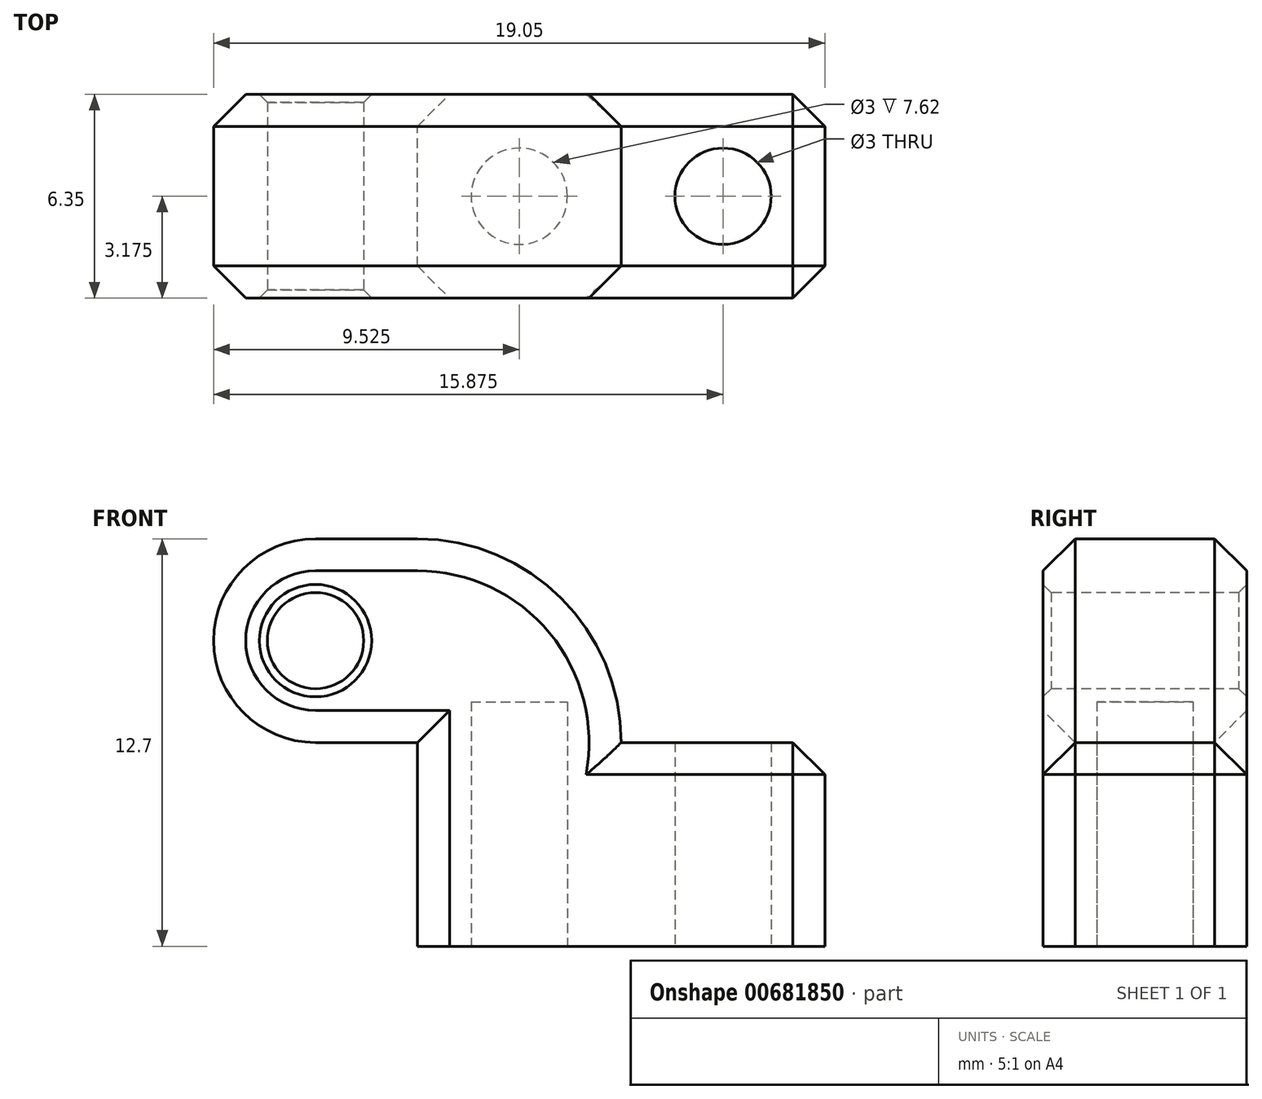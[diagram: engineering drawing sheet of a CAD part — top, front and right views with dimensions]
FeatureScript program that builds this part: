
annotation { "Feature Type Name" : "Feature", "Feature Type Description" : "" }
export const myFeature = defineFeature(function(context is Context, id is Id, definition is map)
    precondition{}
    {
        {
            var Q0;
            Q0=qCreatedBy(makeId("Top.planeOp"),FACE);
            var sketch = newSketch(context, id + "F0", { "sketchPlane" : qUnion([Q0])});
            skLineSegment(sketch, "E0.bottom", {"start": v(0, 0) * mm, "end": v(12.7, 0) * mm});
            skLineSegment(sketch, "E0.top", {"start": v(0, -6.35) * mm, "end": v(12.7, -6.35) * mm});
            skLineSegment(sketch, "E0.left", {"start": v(0, 0) * mm, "end": v(0, -6.35) * mm});
            skLineSegment(sketch, "E0.right", {"start": v(12.7, 0) * mm, "end": v(12.7, -6.35) * mm});
            skSolve(sketch);
        }
        {
            var Q0;
            Q0 = qSketchRegion(id + "F0", true);
            extrude(context, id + "F1", {"entities" : qUnion([Q0]), "depth" : 6.35 * mm, "offsetDistance" : 25.4 * mm});
        }
        {
            var Q0;
            Q0=makeQuery(id+"F1.opExtrude","CAP_FACE",FACE,{"disambiguationData":[OSD([sQuery(id+"F0.wireOp",EDGE,"E0.bottom"),sQuery(id+"F0.wireOp",EDGE,"E0.top"),sQuery(id+"F0.wireOp",EDGE,"E0.left"),sQuery(id+"F0.wireOp",EDGE,"E0.right")])],"isStart":false});
            var sketch = newSketch(context, id + "F2", { "sketchPlane" : qUnion([Q0])});
            skLineSegment(sketch, "E1.bottom", {"start": v(0, 0) * mm, "end": v(6.35, 0) * mm});
            skLineSegment(sketch, "E1.top", {"start": v(0, -6.35) * mm, "end": v(6.35, -6.35) * mm});
            skLineSegment(sketch, "E1.left", {"start": v(0, 0) * mm, "end": v(0, -6.35) * mm});
            skLineSegment(sketch, "E1.right", {"start": v(6.35, 0) * mm, "end": v(6.35, -6.35) * mm});
            skSolve(sketch);
        }
        {
            var Q0;
            Q0 = qSketchRegion(id + "F2", true);
            extrude(context, id + "F3", {"entities" : qUnion([Q0]), "operationType" : NewBodyOperationType.ADD, "depth" : 6.35 * mm, "offsetDistance" : 25.4 * mm});
        }
        {
            var Q0;
            Q0=makeQuery(id+"F3.boolean.opBoolean","MERGE",FACE,{"derivedFrom":[makeQuery(id+"F1.opExtrude","SWEPT_FACE",FACE,{"disambiguationData":[OSD([sQuery(id+"F0.wireOp",EDGE,"E0.left")])]}),makeQuery(id+"F3.opExtrude","SWEPT_FACE",FACE,{"disambiguationData":[OSD([sQuery(id+"F2.wireOp",EDGE,"E1.left")])]})]});
            var sketch = newSketch(context, id + "F4", { "sketchPlane" : qUnion([Q0])});
            skLineSegment(sketch, "E2.bottom", {"start": v(6.35, 12.7) * mm, "end": v(0, 12.7) * mm});
            skLineSegment(sketch, "E2.top", {"start": v(6.35, 6.35) * mm, "end": v(0, 6.35) * mm});
            skLineSegment(sketch, "E2.left", {"start": v(6.35, 12.7) * mm, "end": v(6.35, 6.35) * mm});
            skLineSegment(sketch, "E2.right", {"start": v(0, 12.7) * mm, "end": v(0, 6.35) * mm});
            skSolve(sketch);
        }
        {
            var Q0;
            Q0 = qSketchRegion(id + "F4", true);
            extrude(context, id + "F5", {"entities" : qUnion([Q0]), "operationType" : NewBodyOperationType.ADD, "depth" : 6.35 * mm, "offsetDistance" : 25.4 * mm});
        }
        {
            var Q0;
            Q0=makeQuery(id+"F5.opExtrude","CAP_EDGE",EDGE,{"disambiguationData":[OSD([sQuery(id+"F4.wireOp",EDGE,"E2.bottom")])],"isStart":false});
            var Q1;
            Q1=makeQuery(id+"F5.opExtrude","CAP_EDGE",EDGE,{"disambiguationData":[OSD([sQuery(id+"F4.wireOp",EDGE,"E2.top")])],"isStart":false});
            fillet(context, id + "F6", {"entities" : qUnion([Q0, Q1]), "radius" : 3.17 * mm, "tangentPropagation" : true, "allowEdgeOverflow" : false});
        }
        {
            var Q0;
            Q0=makeQuery(id+"F3.opExtrude","CAP_EDGE",EDGE,{"disambiguationData":[OSD([sQuery(id+"F2.wireOp",EDGE,"E1.right")])],"isStart":false});
            fillet(context, id + "F7", {"entities" : qUnion([Q0]), "radius" : 6.35 * mm, "tangentPropagation" : true, "allowEdgeOverflow" : false});
        }
        {
            var Q0;
            Q0=makeQuery(id+"F5.boolean.opBoolean","MERGE",FACE,{"derivedFrom":[makeQuery(id+"F3.boolean.opBoolean","MERGE",FACE,{"derivedFrom":[makeQuery(id+"F1.opExtrude","SWEPT_FACE",FACE,{"disambiguationData":[OSD([sQuery(id+"F0.wireOp",EDGE,"E0.top")])]}),makeQuery(id+"F3.opExtrude","SWEPT_FACE",FACE,{"disambiguationData":[OSD([sQuery(id+"F2.wireOp",EDGE,"E1.top")])]})]}),makeQuery(id+"F5.opExtrude","SWEPT_FACE",FACE,{"disambiguationData":[OSD([sQuery(id+"F4.wireOp",EDGE,"E2.left")])]})]});
            var sketch = newSketch(context, id + "F8", { "sketchPlane" : qUnion([Q0])});
            skCircle(sketch, "E3", {"center": v(-3.18, 9.53) * mm, "radius": 1.5 * mm});
            skSolve(sketch);
        }
        {
            var Q0;
            Q0 = qSketchRegion(id + "F8", true);
            var Q1;
            Q1=makeQuery(id+"F5.boolean.opBoolean","MERGE",FACE,{"derivedFrom":[makeQuery(id+"F3.boolean.opBoolean","MERGE",FACE,{"derivedFrom":[makeQuery(id+"F1.opExtrude","SWEPT_FACE",FACE,{"disambiguationData":[OSD([sQuery(id+"F0.wireOp",EDGE,"E0.bottom")])]}),makeQuery(id+"F3.opExtrude","SWEPT_FACE",FACE,{"disambiguationData":[OSD([sQuery(id+"F2.wireOp",EDGE,"E1.bottom")])]})]}),makeQuery(id+"F5.opExtrude","SWEPT_FACE",FACE,{"disambiguationData":[OSD([sQuery(id+"F4.wireOp",EDGE,"E2.right")])]})]});
            extrude(context, id + "F9", {"entities" : qUnion([Q0]), "operationType" : NewBodyOperationType.REMOVE, "endBound" : BoundingType.UP_TO_SURFACE, "oppositeDirection" : true, "depth" : 25.4 * mm, "endBoundEntityFace" : qUnion([Q1]), "offsetDistance" : 25.4 * mm});
        }
        {
            var Q0;
            Q0=makeQuery(id+"F1.opExtrude","CAP_FACE",FACE,{"disambiguationData":[OSD([sQuery(id+"F0.wireOp",EDGE,"E0.bottom"),sQuery(id+"F0.wireOp",EDGE,"E0.top"),sQuery(id+"F0.wireOp",EDGE,"E0.left"),sQuery(id+"F0.wireOp",EDGE,"E0.right")])],"isStart":true});
            var sketch = newSketch(context, id + "F10", { "sketchPlane" : qUnion([Q0])});
            skCircle(sketch, "E4", {"center": v(9.53, 3.18) * mm, "radius": 1.5 * mm});
            skPoint(sketch, "E4.centerSnap0", {"position": v(12.7, 3.18) * mm});
            skCircle(sketch, "E5", {"center": v(3.18, 3.18) * mm, "radius": 1.5 * mm});
            skPoint(sketch, "E5.centerSnap0", {"position": v(0, 3.18) * mm});
            skSolve(sketch);
        }
        {
            var Q0;
            Q0 = qSketchRegion(id + "F10", true);
            extrude(context, id + "F11", {"entities" : qUnion([Q0]), "operationType" : NewBodyOperationType.REMOVE, "oppositeDirection" : true, "depth" : 7.62 * mm, "offsetDistance" : 25.4 * mm});
        }
        {
            var Q0;
            Q0=makeQuery(id+"F9.boolean.opBoolean","COPY",FACE,{"derivedFrom":makeQuery(id+"F9.opExtrude","SWEPT_FACE",FACE,{"disambiguationData":[OSD([sQuery(id+"F8.wireOp",EDGE,"E3")])]})});
            chamfer(context, id + "F12", {"entities" : qUnion([Q0]), "width" : .25 * mm, "tangentPropagation" : true});
        }
        {
            var Q0;
            Q0=makeQuery(id+"F6.opFillet","BLEND_EDGE",EDGE,{"blendedFrom":[makeQuery(id+"F5.opExtrude","CAP_EDGE",EDGE,{"disambiguationData":[OSD([sQuery(id+"F4.wireOp",EDGE,"E2.top")])],"isStart":false}),makeQuery(id+"F5.boolean.opBoolean","MERGE",FACE,{"derivedFrom":[makeQuery(id+"F3.boolean.opBoolean","MERGE",FACE,{"derivedFrom":[makeQuery(id+"F1.opExtrude","SWEPT_FACE",FACE,{"disambiguationData":[OSD([sQuery(id+"F0.wireOp",EDGE,"E0.top")])]}),makeQuery(id+"F3.opExtrude","SWEPT_FACE",FACE,{"disambiguationData":[OSD([sQuery(id+"F2.wireOp",EDGE,"E1.top")])]})]}),makeQuery(id+"F5.opExtrude","SWEPT_FACE",FACE,{"disambiguationData":[OSD([sQuery(id+"F4.wireOp",EDGE,"E2.left")])]})]})],"blendedInto":[makeQuery(id+"F5.boolean.opBoolean","MERGE",FACE,{"derivedFrom":[makeQuery(id+"F3.boolean.opBoolean","MERGE",FACE,{"derivedFrom":[makeQuery(id+"F1.opExtrude","SWEPT_FACE",FACE,{"disambiguationData":[OSD([sQuery(id+"F0.wireOp",EDGE,"E0.top")])]}),makeQuery(id+"F3.opExtrude","SWEPT_FACE",FACE,{"disambiguationData":[OSD([sQuery(id+"F2.wireOp",EDGE,"E1.top")])]})]}),makeQuery(id+"F5.opExtrude","SWEPT_FACE",FACE,{"disambiguationData":[OSD([sQuery(id+"F4.wireOp",EDGE,"E2.left")])]})]})]});
            var Q1;
            Q1=makeQuery(id+"F5.opExtrude","SWEPT_EDGE",EDGE,{"disambiguationData":[OSD([sQuery(id+"F0.wireOp",EDGE,"E0.top"),sQuery(id+"F0.wireOp",EDGE,"E0.left"),sQuery(id+"F2.wireOp",EDGE,"E1.top"),sQuery(id+"F2.wireOp",EDGE,"E1.left"),sQuery(id+"F4.wireOp",EDGE,"E2.top"),sQuery(id+"F4.wireOp",EDGE,"E2.left")])]});
            var Q2;
            Q2=makeQuery(id+"F3.boolean.opBoolean","MERGE",EDGE,{"derivedFrom":[makeQuery(id+"F1.opExtrude","SWEPT_EDGE",EDGE,{"disambiguationData":[OSD([sQuery(id+"F0.wireOp",EDGE,"E0.top"),sQuery(id+"F0.wireOp",EDGE,"E0.left")])]}),makeQuery(id+"F3.opExtrude","SWEPT_EDGE",EDGE,{"disambiguationData":[OSD([sQuery(id+"F2.wireOp",EDGE,"E1.top"),sQuery(id+"F2.wireOp",EDGE,"E1.left")])]})]});
            var Q3;
            Q3=makeQuery(id+"F3.boolean.opBoolean","MERGE",EDGE,{"derivedFrom":[makeQuery(id+"F1.opExtrude","SWEPT_EDGE",EDGE,{"disambiguationData":[OSD([sQuery(id+"F0.wireOp",EDGE,"E0.bottom"),sQuery(id+"F0.wireOp",EDGE,"E0.left")])]}),makeQuery(id+"F3.opExtrude","SWEPT_EDGE",EDGE,{"disambiguationData":[OSD([sQuery(id+"F2.wireOp",EDGE,"E1.bottom"),sQuery(id+"F2.wireOp",EDGE,"E1.left")])]})]});
            var Q4;
            Q4=makeQuery(id+"F6.opFillet","BLEND_EDGE",EDGE,{"blendedFrom":[makeQuery(id+"F5.opExtrude","CAP_EDGE",EDGE,{"disambiguationData":[OSD([sQuery(id+"F4.wireOp",EDGE,"E2.top")])],"isStart":false}),makeQuery(id+"F5.boolean.opBoolean","MERGE",FACE,{"derivedFrom":[makeQuery(id+"F3.boolean.opBoolean","MERGE",FACE,{"derivedFrom":[makeQuery(id+"F1.opExtrude","SWEPT_FACE",FACE,{"disambiguationData":[OSD([sQuery(id+"F0.wireOp",EDGE,"E0.bottom")])]}),makeQuery(id+"F3.opExtrude","SWEPT_FACE",FACE,{"disambiguationData":[OSD([sQuery(id+"F2.wireOp",EDGE,"E1.bottom")])]})]}),makeQuery(id+"F5.opExtrude","SWEPT_FACE",FACE,{"disambiguationData":[OSD([sQuery(id+"F4.wireOp",EDGE,"E2.right")])]})]})],"blendedInto":[makeQuery(id+"F5.boolean.opBoolean","MERGE",FACE,{"derivedFrom":[makeQuery(id+"F3.boolean.opBoolean","MERGE",FACE,{"derivedFrom":[makeQuery(id+"F1.opExtrude","SWEPT_FACE",FACE,{"disambiguationData":[OSD([sQuery(id+"F0.wireOp",EDGE,"E0.bottom")])]}),makeQuery(id+"F3.opExtrude","SWEPT_FACE",FACE,{"disambiguationData":[OSD([sQuery(id+"F2.wireOp",EDGE,"E1.bottom")])]})]}),makeQuery(id+"F5.opExtrude","SWEPT_FACE",FACE,{"disambiguationData":[OSD([sQuery(id+"F4.wireOp",EDGE,"E2.right")])]})]})]});
            var Q5;
            Q5=makeQuery(id+"F5.boolean.opBoolean","MERGE",EDGE,{"derivedFrom":[makeQuery(id+"F3.opExtrude","CAP_EDGE",EDGE,{"disambiguationData":[OSD([sQuery(id+"F2.wireOp",EDGE,"E1.top")])],"isStart":false}),makeQuery(id+"F5.opExtrude","SWEPT_EDGE",EDGE,{"disambiguationData":[OSD([sQuery(id+"F4.wireOp",EDGE,"E2.bottom"),sQuery(id+"F4.wireOp",EDGE,"E2.left")])]})]});
            var Q6;
            Q6=makeQuery(id+"F7.opFillet","BLEND_EDGE",EDGE,{"blendedFrom":[makeQuery(id+"F3.opExtrude","CAP_EDGE",EDGE,{"disambiguationData":[OSD([sQuery(id+"F2.wireOp",EDGE,"E1.right")])],"isStart":false}),makeQuery(id+"F5.boolean.opBoolean","MERGE",FACE,{"derivedFrom":[makeQuery(id+"F3.boolean.opBoolean","MERGE",FACE,{"derivedFrom":[makeQuery(id+"F1.opExtrude","SWEPT_FACE",FACE,{"disambiguationData":[OSD([sQuery(id+"F0.wireOp",EDGE,"E0.top")])]}),makeQuery(id+"F3.opExtrude","SWEPT_FACE",FACE,{"disambiguationData":[OSD([sQuery(id+"F2.wireOp",EDGE,"E1.top")])]})]}),makeQuery(id+"F5.opExtrude","SWEPT_FACE",FACE,{"disambiguationData":[OSD([sQuery(id+"F4.wireOp",EDGE,"E2.left")])]})]})],"blendedInto":[makeQuery(id+"F5.boolean.opBoolean","MERGE",FACE,{"derivedFrom":[makeQuery(id+"F3.boolean.opBoolean","MERGE",FACE,{"derivedFrom":[makeQuery(id+"F1.opExtrude","SWEPT_FACE",FACE,{"disambiguationData":[OSD([sQuery(id+"F0.wireOp",EDGE,"E0.top")])]}),makeQuery(id+"F3.opExtrude","SWEPT_FACE",FACE,{"disambiguationData":[OSD([sQuery(id+"F2.wireOp",EDGE,"E1.top")])]})]}),makeQuery(id+"F5.opExtrude","SWEPT_FACE",FACE,{"disambiguationData":[OSD([sQuery(id+"F4.wireOp",EDGE,"E2.left")])]})]})]});
            var Q7;
            Q7=makeQuery(id+"F1.opExtrude","CAP_EDGE",EDGE,{"disambiguationData":[OSD([sQuery(id+"F0.wireOp",EDGE,"E0.top")])],"isStart":false});
            var Q8;
            Q8=makeQuery(id+"F1.opExtrude","CAP_EDGE",EDGE,{"disambiguationData":[OSD([sQuery(id+"F0.wireOp",EDGE,"E0.bottom")])],"isStart":false});
            var Q9;
            Q9=makeQuery(id+"F1.opExtrude","CAP_EDGE",EDGE,{"disambiguationData":[OSD([sQuery(id+"F0.wireOp",EDGE,"E0.right")])],"isStart":false});
            var Q10;
            Q10=makeQuery(id+"F1.opExtrude","SWEPT_EDGE",EDGE,{"disambiguationData":[OSD([sQuery(id+"F0.wireOp",EDGE,"E0.bottom"),sQuery(id+"F0.wireOp",EDGE,"E0.right")])]});
            var Q11;
            Q11=makeQuery(id+"F1.opExtrude","SWEPT_EDGE",EDGE,{"disambiguationData":[OSD([sQuery(id+"F0.wireOp",EDGE,"E0.top"),sQuery(id+"F0.wireOp",EDGE,"E0.right")])]});
            var Q12;
            Q12=makeQuery(id+"F7.opFillet","BLEND_EDGE",EDGE,{"blendedFrom":[makeQuery(id+"F3.opExtrude","CAP_EDGE",EDGE,{"disambiguationData":[OSD([sQuery(id+"F2.wireOp",EDGE,"E1.right")])],"isStart":false}),makeQuery(id+"F5.boolean.opBoolean","MERGE",FACE,{"derivedFrom":[makeQuery(id+"F3.boolean.opBoolean","MERGE",FACE,{"derivedFrom":[makeQuery(id+"F1.opExtrude","SWEPT_FACE",FACE,{"disambiguationData":[OSD([sQuery(id+"F0.wireOp",EDGE,"E0.bottom")])]}),makeQuery(id+"F3.opExtrude","SWEPT_FACE",FACE,{"disambiguationData":[OSD([sQuery(id+"F2.wireOp",EDGE,"E1.bottom")])]})]}),makeQuery(id+"F5.opExtrude","SWEPT_FACE",FACE,{"disambiguationData":[OSD([sQuery(id+"F4.wireOp",EDGE,"E2.right")])]})]})],"blendedInto":[makeQuery(id+"F5.boolean.opBoolean","MERGE",FACE,{"derivedFrom":[makeQuery(id+"F3.boolean.opBoolean","MERGE",FACE,{"derivedFrom":[makeQuery(id+"F1.opExtrude","SWEPT_FACE",FACE,{"disambiguationData":[OSD([sQuery(id+"F0.wireOp",EDGE,"E0.bottom")])]}),makeQuery(id+"F3.opExtrude","SWEPT_FACE",FACE,{"disambiguationData":[OSD([sQuery(id+"F2.wireOp",EDGE,"E1.bottom")])]})]}),makeQuery(id+"F5.opExtrude","SWEPT_FACE",FACE,{"disambiguationData":[OSD([sQuery(id+"F4.wireOp",EDGE,"E2.right")])]})]})]});
            var Q13;
            Q13=makeQuery(id+"F5.opExtrude","SWEPT_EDGE",EDGE,{"disambiguationData":[OSD([sQuery(id+"F0.wireOp",EDGE,"E0.bottom"),sQuery(id+"F0.wireOp",EDGE,"E0.left"),sQuery(id+"F2.wireOp",EDGE,"E1.bottom"),sQuery(id+"F2.wireOp",EDGE,"E1.left"),sQuery(id+"F4.wireOp",EDGE,"E2.top"),sQuery(id+"F4.wireOp",EDGE,"E2.right")])]});
            var Q14;
            Q14=makeQuery(id+"F5.boolean.opBoolean","MERGE",EDGE,{"derivedFrom":[makeQuery(id+"F3.opExtrude","CAP_EDGE",EDGE,{"disambiguationData":[OSD([sQuery(id+"F2.wireOp",EDGE,"E1.bottom")])],"isStart":false}),makeQuery(id+"F5.opExtrude","SWEPT_EDGE",EDGE,{"disambiguationData":[OSD([sQuery(id+"F4.wireOp",EDGE,"E2.bottom"),sQuery(id+"F4.wireOp",EDGE,"E2.right")])]})]});
            chamfer(context, id + "F13", {"entities" : qUnion([Q0, Q1, Q2, Q3, Q4, Q5, Q6, Q7, Q8, Q9, Q10, Q11, Q12, Q13, Q14]), "width" : 1 * mm, "tangentPropagation" : true});
        }
    });
